# Revit family: Gewindeplatte 38x17
name_source: partatom
category: HLS-Bauteile
revit_build: Autodesk Revit 2017 (Build: 20190507_1515(x64)
units: mm (PartAtom-declared; Revit-internal decimal feet)

## family parameters
Arbeitsebenenbasiert = Ja
Beim Laden mit Abzugskörper schneiden = Nein
Bemaßung runder Anschluss = Durchmesser verwenden
Gemeinsam genutzt = Ja
Immer vertikal = Nein
Raumberechnungspunkt = Nein
Teiletyp = Normal

## types (3) — shared parameters
Breite = 18 mm  [stored 0.0590551 ft]
Fabrikat = MEFA
Firma = MEFA Befestigungs- und Montagesysteme GmbH
Gewicht = 0.02 kg
Gewicht pro Bauteil = 0.02 kg
Kurztext1 = Gewindeplatte
Länge = 35 mm  [stored 0.114829 ft]
Material = Stahl
Materialname = S235
Mengeneinheit = St
Oberflaeche = galvanisch verzinkt
Profiltyp = 35, Stex 35
Vorgabe-Ansicht = 1219 mm
vpe = 100 St
zero-valued in all types: Stärke

## per-type parameters (varying)
| type | Artikelnummer | EAN | Kurztext2 | d2 |
| MEFA Gewindeplatte 38x17 M10 | 0750085 | 4250928417145 | M10 38x17 gvz | 4 mm  [stored 0.0131234 ft] |
| MEFA Gewindeplatte 38x17 M 8 | 0750077 | 4250928417138 | M8 38x17 gvz | 3 mm  [stored 0.00984252 ft] |
| MEFA Gewindeplatte 38x17 M12 | 0750093 | 4250928417152 | M12 38x17 gvz | 5 mm  [stored 0.0164042 ft] |

note: [stored X ft] marks values corroborated as IEEE doubles in the binary element streams (Revit-internal decimal feet)
